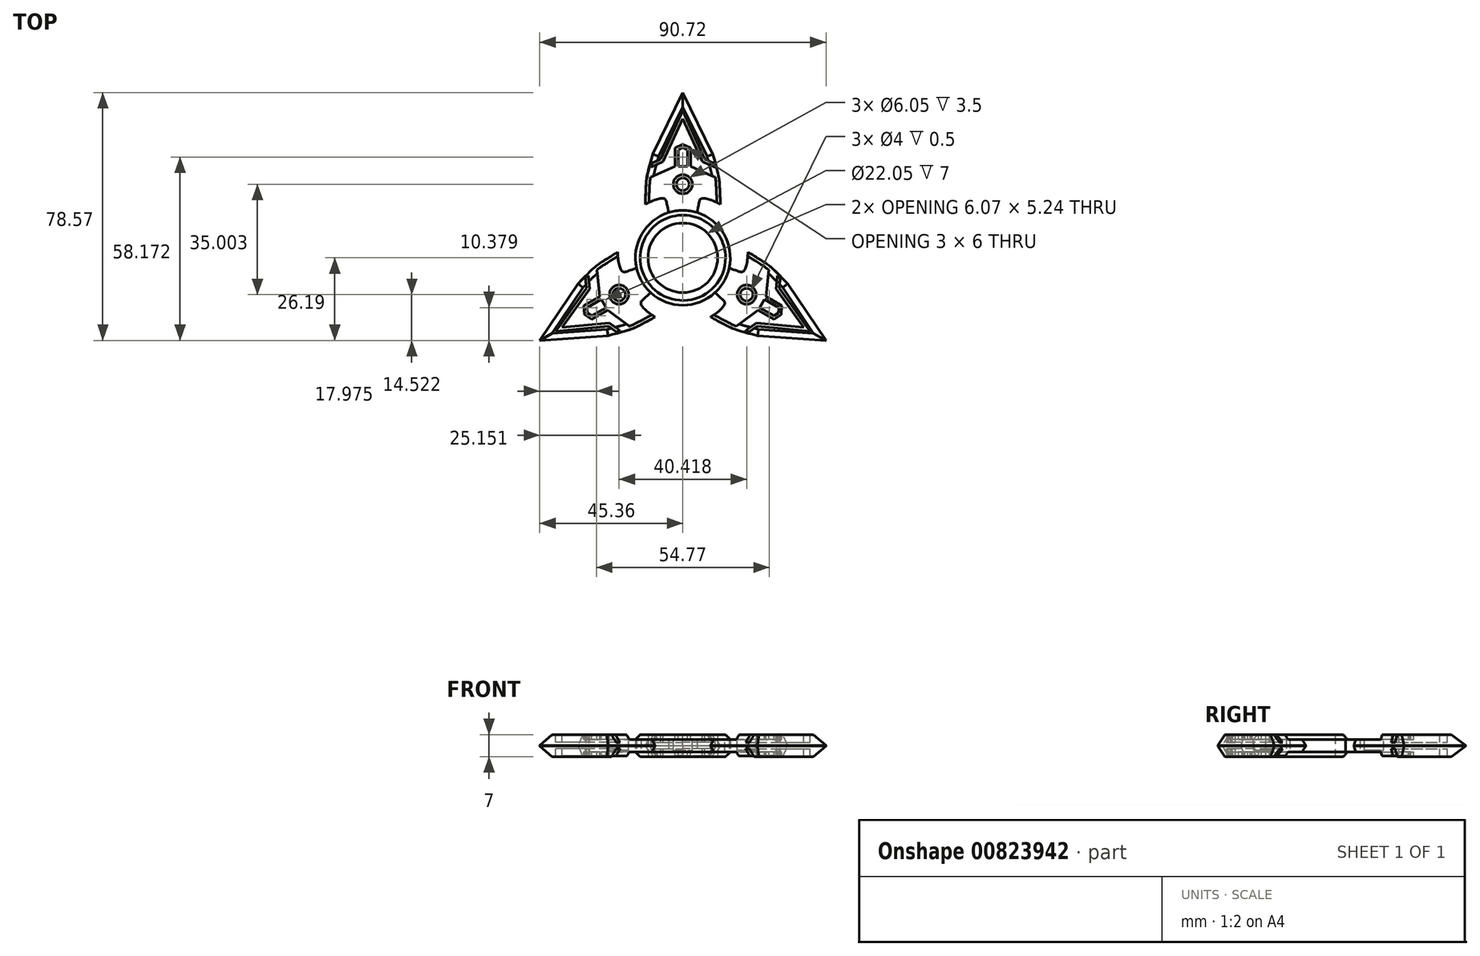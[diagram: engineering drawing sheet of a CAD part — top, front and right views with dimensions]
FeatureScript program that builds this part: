
annotation { "Feature Type Name" : "Feature", "Feature Type Description" : "" }
export const myFeature = defineFeature(function(context is Context, id is Id, definition is map)
    precondition{}
    {
        {
            var Q0;
            Q0=qCreatedBy(makeId("Top.planeOp"),FACE);
            var sketch = newSketch(context, id + "F0", { "sketchPlane" : qUnion([Q0])});
            skCircle(sketch, "E0", {"center": v(0, 0) * mm, "radius": 11.03 * mm});
            skCircle(sketch, "E1", {"center": v(0, 0) * mm, "radius": 15.03 * mm});
            skLineSegment(sketch, "E2", {"start": v(0, 0) * mm, "end": v(0, 55.55) * mm, "construction": true});
            skFitSpline(sketch, "E3", {"points": [v(-4.5, 14.34) * mm, v(-5.85, 18.75) * mm, v(-11.84, 16.98) * mm], "startDerivative": vector(-4.32, 19.26) * mm, "endDerivative": vector(-16.85, -9) * mm});
            skFitSpline(sketch, "E4", {"points": [v(-11.84, 16.98) * mm, v(-11.67, 22.7) * mm, v(-9.52, 32.86) * mm], "startDerivative": vector(-0.35, 14.64) * mm, "endDerivative": vector(11.12, 38.92) * mm});
            skLineSegment(sketch, "E5", {"start": v(-9.52, 32.86) * mm, "end": v(0, 52.38) * mm});
            skCircle(sketch, "E6", {"center": v(0, 0) * mm, "radius": 52.38 * mm, "construction": true});
            skLineSegment(sketch, "E7.MirrorCS", {"start": v(9.52, 32.86) * mm, "end": v(0, 52.38) * mm});
            skLineSegment(sketch, "E8.MirrorCS", {"start": v(0, 0) * mm, "end": v(0, 55.55) * mm});
            skFitSpline(sketch, "E9.MirrorCS", {"points": [v(11.84, 16.98) * mm, v(11.67, 22.7) * mm, v(9.52, 32.86) * mm], "startDerivative": vector(0.35, 14.64) * mm, "endDerivative": vector(-11.12, 38.92) * mm});
            skFitSpline(sketch, "E10.MirrorCS", {"points": [v(4.5, 14.34) * mm, v(5.85, 18.75) * mm, v(11.84, 16.98) * mm], "startDerivative": vector(4.32, 19.26) * mm, "endDerivative": vector(16.85, -9) * mm});
            skSolve(sketch);
        }
        {
            var Q0;
            Q0 = qSketchRegion(id + "F0", true);
            extrude(context, id + "F1", {"entities" : qUnion([Q0]), "depth" : 7 * mm, "offsetDistance" : 25 * mm});
        }
        {
            var Q0;
            Q0=makeQuery(id+"F1.opExtrude","CAP_FACE",FACE,{"disambiguationData":[OSD([sQuery(id+"F0.wireOp",EDGE,"E0"),sQuery(id+"F0.wireOp",EDGE,"E1"),sQuery(id+"F0.wireOp",EDGE,"E3"),sQuery(id+"F0.wireOp",EDGE,"E4"),sQuery(id+"F0.wireOp",EDGE,"E5"),sQuery(id+"F0.wireOp",EDGE,"E7.MirrorCS"),sQuery(id+"F0.wireOp",EDGE,"E9.MirrorCS"),sQuery(id+"F0.wireOp",EDGE,"E10.MirrorCS")])],"isStart":false});
            var sketch = newSketch(context, id + "F2", { "sketchPlane" : qUnion([Q0])});
            skLineSegment(sketch, "E11", {"start": v(-11.5, 24.98) * mm, "end": v(-2.5, 28.98) * mm});
            skLineSegment(sketch, "E12", {"start": v(-2.5, 28.98) * mm, "end": v(2.5, 28.98) * mm, "construction": true});
            skLineSegment(sketch, "E13", {"start": v(2.5, 28.98) * mm, "end": v(11.5, 24.98) * mm});
            skLineSegment(sketch, "E14", {"start": v(2.5, 28.98) * mm, "end": v(2.5, 34.78) * mm});
            skLineSegment(sketch, "E15", {"start": v(2.5, 34.78) * mm, "end": v(0, 35.98) * mm});
            skLineSegment(sketch, "E16", {"start": v(0, 35.98) * mm, "end": v(-2.5, 34.78) * mm});
            skLineSegment(sketch, "E17", {"start": v(-2.5, 34.78) * mm, "end": v(-2.5, 28.98) * mm});
            skLineSegment(sketch, "E18", {"start": v(-10.72, 28.48) * mm, "end": v(-6.22, 30.48) * mm});
            skLineSegment(sketch, "E19", {"start": v(-6.22, 30.48) * mm, "end": v(0, 44.17) * mm});
            skLineSegment(sketch, "E20.MirrorCS", {"start": v(6.22, 30.48) * mm, "end": v(0, 44.17) * mm});
            skLineSegment(sketch, "E21.MirrorCS", {"start": v(10.72, 28.48) * mm, "end": v(6.22, 30.48) * mm});
            skLineSegment(sketch, "E22", {"start": v(-11.5, 24.98) * mm, "end": v(-14.66, 14.59) * mm});
            skLineSegment(sketch, "E23", {"start": v(-14.66, 14.59) * mm, "end": v(-4.5, 14.34) * mm});
            skLineSegment(sketch, "E24", {"start": v(-4.5, 14.34) * mm, "end": v(4.5, 14.34) * mm});
            skLineSegment(sketch, "E25", {"start": v(4.5, 14.34) * mm, "end": v(14.6, 14.32) * mm});
            skLineSegment(sketch, "E26", {"start": v(14.6, 14.32) * mm, "end": v(11.5, 24.98) * mm});
            skLineSegment(sketch, "E27", {"start": v(0, 34.98) * mm, "end": v(-1.5, 34.26) * mm});
            skLineSegment(sketch, "E28", {"start": v(-1.5, 34.26) * mm, "end": v(-1.5, 28.98) * mm});
            skLineSegment(sketch, "E29.MirrorCS", {"start": v(1.5, 34.26) * mm, "end": v(1.5, 28.98) * mm});
            skLineSegment(sketch, "E30.MirrorCS", {"start": v(0, 34.98) * mm, "end": v(1.5, 34.26) * mm});
            skLineSegment(sketch, "E31", {"start": v(-1.5, 28.98) * mm, "end": v(1.5, 28.98) * mm});
            skLineSegment(sketch, "E32", {"start": v(-10.4, 29.72) * mm, "end": v(-6.98, 31.24) * mm});
            skLineSegment(sketch, "E33", {"start": v(-6.98, 31.24) * mm, "end": v(0, 46.6) * mm});
            skLineSegment(sketch, "E34.MirrorCS", {"start": v(6.98, 31.24) * mm, "end": v(0, 46.6) * mm});
            skLineSegment(sketch, "E35.MirrorCS", {"start": v(10.4, 29.72) * mm, "end": v(6.98, 31.24) * mm});
            skLineSegment(sketch, "E36", {"start": v(-19.07, 25.86) * mm, "end": v(-18.66, 24.95) * mm, "construction": true});
            skLineSegment(sketch, "E37", {"start": v(-6.52, 32.25) * mm, "end": v(-5.6, 31.83) * mm, "construction": true});
            skLineSegment(sketch, "E38", {"start": v(6, 30.97) * mm, "end": v(6.9, 31.39) * mm, "construction": true});
            skLineSegment(sketch, "E39", {"start": v(16.98, 25.7) * mm, "end": v(17.38, 26.61) * mm, "construction": true});
            skLineSegment(sketch, "E40", {"start": v(1.5, 31.62) * mm, "end": v(2.5, 31.62) * mm, "construction": true});
            skLineSegment(sketch, "E41", {"start": v(0, 34.98) * mm, "end": v(0, 35.98) * mm, "construction": true});
            skSolve(sketch);
        }
        {
            var Q0;
            Q0 = qSketchRegion(id + "F2", true);
            extrude(context, id + "F3", {"entities" : qUnion([Q0]), "operationType" : NewBodyOperationType.REMOVE, "oppositeDirection" : true, "depth" : 1.5 * mm, "offsetDistance" : 25 * mm});
        }
        {
            var Q0;
            Q0=qCreatedBy(makeId("Front.planeOp"),FACE);
            cPlane(context, id + "F4", {"entities" : qUnion([Q0]), "cplaneType" : CPlaneType.OFFSET, "offset" : 50.42 * mm, "oppositeDirection" : true, "width" : 150 * mm, "height" : 150 * mm});
        }
        {
            var Q0;
            {var subQ2=sQuery(id+"F2.wireOp",EDGE,"E18");Q0=makeQuery(id+"F2.imprint","IMPRINT",FACE,{"disambiguationData":[TD([[makeQuery(id+"F2.imprint","IMPRINT",EDGE,{"derivedFrom":subQ2}),1.0]])]});}
            extrude(context, id + "F5", {"entities" : qUnion([Q0]), "operationType" : NewBodyOperationType.REMOVE, "oppositeDirection" : true, "depth" : 2.5 * mm, "offsetDistance" : 25 * mm});
        }
        {
            var Q0;
            Q0=qCreatedBy(makeId("Front.planeOp"),FACE);
            var sketch = newSketch(context, id + "F6", { "sketchPlane" : qUnion([Q0])});
            skLineSegment(sketch, "E42", {"start": v(0, 0) * mm, "end": v(0, 42.03) * mm, "construction": true});
            skSolve(sketch);
        }
        {
            var Q0;
            {var subQ0=sQuery(id+"F2.wireOp",EDGE,"E11");Q0=makeQuery(id+"F2.imprint","IMPRINT",FACE,{"disambiguationData":[TD([[makeQuery(id+"F2.imprint","IMPRINT",EDGE,{"derivedFrom":subQ0}),-1.0]])]});}
            extrude(context, id + "F7", {"entities" : qUnion([Q0]), "operationType" : NewBodyOperationType.REMOVE, "oppositeDirection" : true, "depth" : 7 * mm, "offsetDistance" : 25 * mm, "hasSecondDirection" : true, "secondDirectionOppositeDirection" : false, "secondDirectionDepth" : -5.5 * mm});
        }
        {
            var Q0;
            {var subQ2=sQuery(id+"F2.wireOp",EDGE,"E18");Q0=makeQuery(id+"F2.imprint","IMPRINT",FACE,{"disambiguationData":[TD([[makeQuery(id+"F2.imprint","IMPRINT",EDGE,{"derivedFrom":subQ2}),1.0]])]});}
            extrude(context, id + "F8", {"entities" : qUnion([Q0]), "operationType" : NewBodyOperationType.REMOVE, "oppositeDirection" : true, "depth" : 25 * mm, "offsetDistance" : 25 * mm, "hasSecondDirection" : true, "secondDirectionOppositeDirection" : true, "secondDirectionDepth" : 4.5 * mm});
        }
        {
            var Q0;
            {var subQ4=sQuery(id+"F0.wireOp",EDGE,"E4");var subQ5=makeQuery(id+"F1.opExtrude","SWEPT_FACE",FACE,{"disambiguationData":[OSD([subQ4])]});var subQ6=sQuery(id+"F0.wireOp",EDGE,"E9.MirrorCS");var subQ8=makeQuery(id+"F7.opExtrude","SWEPT_FACE",FACE,{"disambiguationData":[OSD([sQuery(id+"F2.wireOp",EDGE,"E11")])]});var subQ10=sQuery(id+"F0.wireOp",EDGE,"E7.MirrorCS");var subQ11=sQuery(id+"F0.wireOp",EDGE,"E5");Q0=makeQuery(id+"F8.boolean.opBoolean","SPLIT",FACE,{"disambiguationData":[TD([makeQuery(id+"F7.boolean.opBoolean","COPY",FACE,{"derivedFrom":subQ8})])],"derivedFrom":makeQuery(id+"F7.boolean.opBoolean","SPLIT",FACE,{"disambiguationData":[TD([subQ5])],"derivedFrom":makeQuery(id+"F1.opExtrude","CAP_FACE",FACE,{"disambiguationData":[OSD([sQuery(id+"F0.wireOp",EDGE,"E0"),sQuery(id+"F0.wireOp",EDGE,"E1"),sQuery(id+"F0.wireOp",EDGE,"E3"),subQ4,subQ11,subQ10,subQ6,sQuery(id+"F0.wireOp",EDGE,"E10.MirrorCS")])],"isStart":true})})});}
            var Q1;
            Q1=makeQuery(id+"F7.boolean.opBoolean","SPLIT",FACE,{"disambiguationData":[TD([makeQuery(id+"F7.opExtrude","SWEPT_FACE",FACE,{"disambiguationData":[OSD([sQuery(id+"F2.wireOp",EDGE,"E27")])]})])],"derivedFrom":makeQuery(id+"F1.opExtrude","CAP_FACE",FACE,{"disambiguationData":[OSD([sQuery(id+"F0.wireOp",EDGE,"E0"),sQuery(id+"F0.wireOp",EDGE,"E1"),sQuery(id+"F0.wireOp",EDGE,"E3"),sQuery(id+"F0.wireOp",EDGE,"E4"),sQuery(id+"F0.wireOp",EDGE,"E5"),sQuery(id+"F0.wireOp",EDGE,"E7.MirrorCS"),sQuery(id+"F0.wireOp",EDGE,"E9.MirrorCS"),sQuery(id+"F0.wireOp",EDGE,"E10.MirrorCS")])],"isStart":true})});
            extrude(context, id + "F9", {"entities" : qUnion([Q0, Q1]), "operationType" : NewBodyOperationType.REMOVE, "oppositeDirection" : true, "depth" : 0.2 * mm, "offsetDistance" : 25 * mm});
        }
        {
            var Q0;
            Q0=makeQuery(id+"F1.opExtrude","CAP_EDGE",EDGE,{"disambiguationData":[OSD([sQuery(id+"F0.wireOp",EDGE,"E7.MirrorCS")])],"isStart":true});
            var Q1;
            {var subQ0=sQuery(id+"F0.wireOp",EDGE,"E9.MirrorCS");var subQ1=sQuery(id+"F0.wireOp",EDGE,"E7.MirrorCS");Q1=makeQuery(id+"F8.boolean.opBoolean","SPLIT",EDGE,{"disambiguationData":[TD([makeQuery(id+"F1.opExtrude","SWEPT_FACE",FACE,{"disambiguationData":[OSD([subQ1])]})])],"derivedFrom":makeQuery(id+"F1.opExtrude","CAP_EDGE",EDGE,{"disambiguationData":[OSD([subQ0])],"isStart":true})});}
            var Q2;
            {var subQ0=sQuery(id+"F0.wireOp",EDGE,"E5");var subQ1=sQuery(id+"F0.wireOp",EDGE,"E4");Q2=makeQuery(id+"F8.boolean.opBoolean","SPLIT",EDGE,{"disambiguationData":[TD([makeQuery(id+"F1.opExtrude","SWEPT_FACE",FACE,{"disambiguationData":[OSD([subQ0])]})])],"derivedFrom":makeQuery(id+"F1.opExtrude","CAP_EDGE",EDGE,{"disambiguationData":[OSD([subQ1])],"isStart":true})});}
            var Q3;
            Q3=makeQuery(id+"F1.opExtrude","CAP_EDGE",EDGE,{"disambiguationData":[OSD([sQuery(id+"F0.wireOp",EDGE,"E5")])],"isStart":true});
            chamfer(context, id + "F10", {"entities" : qUnion([Q0, Q1, Q2, Q3]), "chamferType" : ChamferType.TWO_OFFSETS, "width1" : 3.4 * mm, "oppositeDirection" : false, "width2" : 2 * mm, "tangentPropagation" : true});
        }
        {
            var Q0;
            Q0=makeQuery(id+"F1.opExtrude","CAP_EDGE",EDGE,{"disambiguationData":[OSD([sQuery(id+"F0.wireOp",EDGE,"E5")])],"isStart":false});
            var Q1;
            {var subQ0=sQuery(id+"F0.wireOp",EDGE,"E5");var subQ1=sQuery(id+"F0.wireOp",EDGE,"E4");Q1=makeQuery(id+"F5.boolean.opBoolean","SPLIT",EDGE,{"disambiguationData":[TD([makeQuery(id+"F1.opExtrude","SWEPT_FACE",FACE,{"disambiguationData":[OSD([subQ0])]})])],"derivedFrom":makeQuery(id+"F1.opExtrude","CAP_EDGE",EDGE,{"disambiguationData":[OSD([subQ1])],"isStart":false})});}
            var Q2;
            Q2=makeQuery(id+"F1.opExtrude","CAP_EDGE",EDGE,{"disambiguationData":[OSD([sQuery(id+"F0.wireOp",EDGE,"E7.MirrorCS")])],"isStart":false});
            var Q3;
            {var subQ0=sQuery(id+"F0.wireOp",EDGE,"E9.MirrorCS");var subQ1=sQuery(id+"F0.wireOp",EDGE,"E7.MirrorCS");Q3=makeQuery(id+"F5.boolean.opBoolean","SPLIT",EDGE,{"disambiguationData":[TD([makeQuery(id+"F1.opExtrude","SWEPT_FACE",FACE,{"disambiguationData":[OSD([subQ1])]})])],"derivedFrom":makeQuery(id+"F1.opExtrude","CAP_EDGE",EDGE,{"disambiguationData":[OSD([subQ0])],"isStart":false})});}
            chamfer(context, id + "F11", {"entities" : qUnion([Q0, Q1, Q2, Q3]), "chamferType" : ChamferType.TWO_OFFSETS, "width1" : 3.4 * mm, "oppositeDirection" : false, "width2" : 2 * mm, "tangentPropagation" : true});
        }
        {
            var Q0;
            {var subQ0=sQuery(id+"F0.wireOp",EDGE,"E10.MirrorCS");var subQ1=sQuery(id+"F0.wireOp",EDGE,"E9.MirrorCS");var subQ2=sQuery(id+"F0.wireOp",EDGE,"E7.MirrorCS");var subQ3=sQuery(id+"F0.wireOp",EDGE,"E5");var subQ4=sQuery(id+"F0.wireOp",EDGE,"E4");var subQ5=sQuery(id+"F0.wireOp",EDGE,"E3");var subQ6=sQuery(id+"F0.wireOp",EDGE,"E1");var subQ7=sQuery(id+"F0.wireOp",EDGE,"E0");Q0=makeQuery(id+"F9.boolean.opBoolean","COPY",FACE,{"derivedFrom":makeQuery(id+"F9.opExtrude","CAP_FACE",FACE,{"disambiguationData":[OSD([subQ7,subQ6,subQ5,subQ4,subQ3,subQ2,subQ1,subQ0]),TDD([makeQuery(id+"F7.boolean.opBoolean","SPLIT",FACE,{"disambiguationData":[TD([makeQuery(id+"F7.opExtrude","SWEPT_FACE",FACE,{"disambiguationData":[OSD([sQuery(id+"F2.wireOp",EDGE,"E27")])]})])],"derivedFrom":makeQuery(id+"F1.opExtrude","CAP_FACE",FACE,{"disambiguationData":[OSD([subQ7,subQ6,subQ5,subQ4,subQ3,subQ2,subQ1,subQ0])],"isStart":true})})])],"isStart":false})});}
            extrude(context, id + "F12", {"entities" : qUnion([Q0]), "operationType" : NewBodyOperationType.REMOVE, "oppositeDirection" : true, "depth" : 0.2 * mm, "offsetDistance" : 25 * mm});
        }
        {
            var Q0;
            Q0=makeQuery(id+"F3.boolean.opBoolean","COPY",FACE,{"derivedFrom":makeQuery(id+"F3.opExtrude","CAP_FACE",FACE,{"disambiguationData":[OSD([sQuery(id+"F2.wireOp",EDGE,"E11"),sQuery(id+"F2.wireOp",EDGE,"E13"),sQuery(id+"F2.wireOp",EDGE,"E14"),sQuery(id+"F2.wireOp",EDGE,"E15"),sQuery(id+"F2.wireOp",EDGE,"E16"),sQuery(id+"F2.wireOp",EDGE,"E17"),sQuery(id+"F2.wireOp",EDGE,"E22"),sQuery(id+"F2.wireOp",EDGE,"E23"),sQuery(id+"F2.wireOp",EDGE,"E24"),sQuery(id+"F2.wireOp",EDGE,"E25"),sQuery(id+"F2.wireOp",EDGE,"E26"),sQuery(id+"F2.wireOp",EDGE,"E27"),sQuery(id+"F2.wireOp",EDGE,"E28"),sQuery(id+"F2.wireOp",EDGE,"E29.MirrorCS"),sQuery(id+"F2.wireOp",EDGE,"E30.MirrorCS"),sQuery(id+"F2.wireOp",EDGE,"E31")])],"isStart":false})});
            var sketch = newSketch(context, id + "F13", { "sketchPlane" : qUnion([Q0])});
            skPoint(sketch, "E43.0.midPoint", {"position": v(-4.87, 19.77) * mm});
            skCircle(sketch, "E44", {"center": v(0, 23.34) * mm, "radius": 3.02 * mm});
            skPoint(sketch, "E44.centerSnap0", {"position": v(0, 14.34) * mm});
            skSolve(sketch);
        }
        {
            var Q0;
            Q0=makeQuery(id+"F13.imprint","IMPRINT",FACE,{"disambiguationData":[TD([[makeQuery(id+"F13.imprint","IMPRINT",EDGE,{"derivedFrom":sQuery(id+"F13.wireOp",EDGE,"E44")}),1.0]])]});
            extrude(context, id + "F14", {"entities" : qUnion([Q0]), "operationType" : NewBodyOperationType.REMOVE, "endBound" : BoundingType.THROUGH_ALL, "oppositeDirection" : true, "depth" : 25 * mm, "offsetDistance" : 25 * mm});
        }
        {
            var Q0;
            Q0=makeQuery(id+"F7.boolean.opBoolean","COPY",FACE,{"derivedFrom":makeQuery(id+"F7.opExtrude","CAP_FACE",FACE,{"disambiguationData":[OSD([sQuery(id+"F0.wireOp",EDGE,"E3"),sQuery(id+"F0.wireOp",EDGE,"E4"),sQuery(id+"F0.wireOp",EDGE,"E9.MirrorCS"),sQuery(id+"F0.wireOp",EDGE,"E10.MirrorCS"),sQuery(id+"F2.wireOp",EDGE,"E11"),sQuery(id+"F2.wireOp",EDGE,"E13"),sQuery(id+"F2.wireOp",EDGE,"E14"),sQuery(id+"F2.wireOp",EDGE,"E15"),sQuery(id+"F2.wireOp",EDGE,"E16"),sQuery(id+"F2.wireOp",EDGE,"E17"),sQuery(id+"F2.wireOp",EDGE,"E24"),sQuery(id+"F2.wireOp",EDGE,"E27"),sQuery(id+"F2.wireOp",EDGE,"E28"),sQuery(id+"F2.wireOp",EDGE,"E29.MirrorCS"),sQuery(id+"F2.wireOp",EDGE,"E30.MirrorCS"),sQuery(id+"F2.wireOp",EDGE,"E31")])],"isStart":true})});
            var sketch = newSketch(context, id + "F15", { "sketchPlane" : qUnion([Q0])});
            skCircle(sketch, "E45", {"center": v(0, -23.34) * mm, "radius": 3.02 * mm});
            skCircle(sketch, "E46", {"center": v(0, -23.34) * mm, "radius": 2 * mm});
            skSolve(sketch);
        }
        {
            var Q0;
            Q0=makeQuery(id+"F15.imprint","IMPRINT",FACE,{"disambiguationData":[TD([[makeQuery(id+"F15.imprint","IMPRINT",EDGE,{"derivedFrom":sQuery(id+"F15.wireOp",EDGE,"E45")}),-1.0]])]});
            extrude(context, id + "F16", {"entities" : qUnion([Q0]), "operationType" : NewBodyOperationType.ADD, "oppositeDirection" : true, "depth" : 0.5 * mm, "offsetDistance" : 25 * mm});
        }
        {
            var Q0;
            Q0=makeQuery(id+"F1.opExtrude","SWEPT_BODY",BODY,{"disambiguationData":[OSD([sQuery(id+"F0.wireOp",EDGE,"E0"),sQuery(id+"F0.wireOp",EDGE,"E1"),sQuery(id+"F0.wireOp",EDGE,"E3"),sQuery(id+"F0.wireOp",EDGE,"E4"),sQuery(id+"F0.wireOp",EDGE,"E5"),sQuery(id+"F0.wireOp",EDGE,"E7.MirrorCS"),sQuery(id+"F0.wireOp",EDGE,"E9.MirrorCS"),sQuery(id+"F0.wireOp",EDGE,"E10.MirrorCS")])]});
            var Q1;
            Q1=sQuery(id+"F6.wireOp",EDGE,"E42");
            circularPattern(context, id + "F17", {"operationType" : NewBodyOperationType.ADD, "entities" : qUnion([Q0]), "axis" : qUnion([Q1]), "angle" : 360 * degree, "instanceCount" : 3, "equalSpace" : true, "fullFeaturePattern" : false});
        }
        {
            var Q0;
            {var subQ0=makeQuery(id+"F1.opExtrude","CAP_EDGE",EDGE,{"disambiguationData":[OSD([sQuery(id+"F0.wireOp",EDGE,"E1")])],"isStart":false});Q0=makeQuery(id+"F17.boolean.opBoolean","MERGE",EDGE,{"derivedFrom":[subQ0,makeQuery(id+"F17.opPattern","COPY",EDGE,{"derivedFrom":subQ0,"instanceName":"1"}),makeQuery(id+"F17.opPattern","COPY",EDGE,{"derivedFrom":subQ0,"instanceName":"2"})]});}
            var Q1;
            {var subQ0=makeQuery(id+"F1.opExtrude","CAP_EDGE",EDGE,{"disambiguationData":[OSD([sQuery(id+"F0.wireOp",EDGE,"E1")])],"isStart":true});Q1=makeQuery(id+"F17.boolean.opBoolean","MERGE",EDGE,{"derivedFrom":[subQ0,makeQuery(id+"F17.opPattern","COPY",EDGE,{"derivedFrom":subQ0,"instanceName":"1"}),makeQuery(id+"F17.opPattern","COPY",EDGE,{"derivedFrom":subQ0,"instanceName":"2"})]});}
            chamfer(context, id + "F18", {"entities" : qUnion([Q0, Q1]), "width" : 1.5 * mm, "tangentPropagation" : true});
        }
    });
